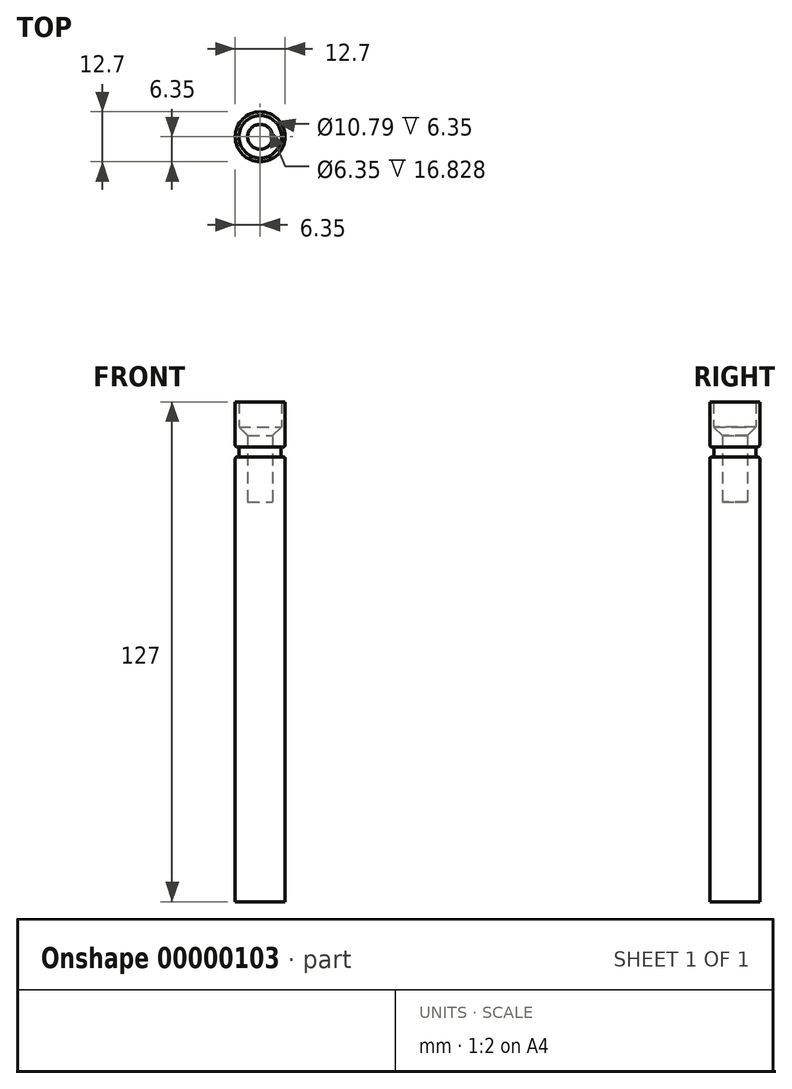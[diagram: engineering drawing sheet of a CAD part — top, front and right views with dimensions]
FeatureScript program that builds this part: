
annotation { "Feature Type Name" : "Feature", "Feature Type Description" : "" }
export const myFeature = defineFeature(function(context is Context, id is Id, definition is map)
    precondition{}
    {
        {
            var Q0;
            Q0=qCreatedBy(makeId("Top.planeOp"),FACE);
            var sketch = newSketch(context, id + "F0", { "sketchPlane" : qUnion([Q0])});
            skCircle(sketch, "E0", {"center": v(0, 0) * mm, "radius": 6.35 * mm});
            skSolve(sketch);
        }
        {
            var Q0;
            Q0=makeQuery(id+"F0.imprint","IMPRINT",FACE,{"disambiguationData":[TD([[makeQuery(id+"F0.imprint","IMPRINT",EDGE,{"derivedFrom":sQuery(id+"F0.wireOp",EDGE,"E0")}),1.0]])]});
            extrude(context, id + "F1", {"entities" : qUnion([Q0]), "depth" : 127 * mm});
        }
        {
            var Q0;
            Q0=qCreatedBy(makeId("Front.planeOp"),FACE);
            var sketch = newSketch(context, id + "F2", { "sketchPlane" : qUnion([Q0])});
            skLineSegment(sketch, "E1.rect.bottom", {"start": v(7.37, 115.57) * mm, "end": v(5.33, 115.57) * mm});
            skLineSegment(sketch, "E1.rect.top", {"start": v(7.37, 113.03) * mm, "end": v(5.33, 113.03) * mm});
            skLineSegment(sketch, "E1.rect.left", {"start": v(7.37, 115.57) * mm, "end": v(7.37, 113.03) * mm});
            skLineSegment(sketch, "E1.rect.right", {"start": v(5.33, 115.57) * mm, "end": v(5.33, 113.03) * mm});
            skPoint(sketch, "E1.rect.middle", {"position": v(6.35, 114.3) * mm});
            skLineSegment(sketch, "E2", {"start": v(0, 127.05) * mm, "end": v(0, 0) * mm, "construction": true});
            skSolve(sketch);
        }
        {
            var Q0;
            Q0=makeQuery(id+"F2.imprint","IMPRINT",FACE,{"disambiguationData":[TD([[makeQuery(id+"F2.imprint","IMPRINT",EDGE,{"derivedFrom":sQuery(id+"F2.wireOp",EDGE,"E1.rect.bottom")}),1.0]])]});
            var Q1;
            Q1=sQuery(id+"F2.wireOp",EDGE,"E2");
            revolve(context, id + "F3", {"operationType" : NewBodyOperationType.REMOVE, "entities" : qUnion([Q0]), "axis" : qUnion([Q1]), "revolveType" : RevolveType.FULL, "oppositeDirection" : true});
        }
        {
            var Q0;
            Q0=makeQuery(id+"F3.opRevolve","SWEPT_EDGE",EDGE,{"disambiguationData":[OSD([sQuery(id+"F2.wireOp",EDGE,"E1.rect.bottom"),sQuery(id+"F2.wireOp",EDGE,"E1.rect.right")])]});
            var Q1;
            Q1=makeQuery(id+"F3.opRevolve","SWEPT_EDGE",EDGE,{"disambiguationData":[OSD([sQuery(id+"F2.wireOp",EDGE,"E1.rect.top"),sQuery(id+"F2.wireOp",EDGE,"E1.rect.right")])]});
            var Q2;
            Q2=makeQuery(id+"F3.boolean.opBoolean","INTERSECT",EDGE,{"derivedFrom":[makeQuery(id+"F1.opExtrude","SWEPT_FACE",FACE,{"disambiguationData":[OSD([sQuery(id+"F0.wireOp",EDGE,"E0")])]}),makeQuery(id+"F3.opRevolve","SWEPT_FACE",FACE,{"disambiguationData":[OSD([sQuery(id+"F2.wireOp",EDGE,"E1.rect.bottom")])]})]});
            var Q3;
            Q3=makeQuery(id+"F3.boolean.opBoolean","INTERSECT",EDGE,{"derivedFrom":[makeQuery(id+"F1.opExtrude","SWEPT_FACE",FACE,{"disambiguationData":[OSD([sQuery(id+"F0.wireOp",EDGE,"E0")])]}),makeQuery(id+"F3.opRevolve","SWEPT_FACE",FACE,{"disambiguationData":[OSD([sQuery(id+"F2.wireOp",EDGE,"E1.rect.top")])]})]});
            fillet(context, id + "F4", {"entities" : qUnion([Q0, Q1, Q2, Q3]), "radius" : 0.5 * mm, "tangentPropagation" : true, "allowEdgeOverflow" : false});
        }
        {
            var Q0;
            Q0=qCreatedBy(makeId("Front.planeOp"),FACE);
            var sketch = newSketch(context, id + "F5", { "sketchPlane" : qUnion([Q0])});
            skLineSegment(sketch, "E3", {"start": v(0, 127) * mm, "end": v(0, 0) * mm, "construction": true});
            skLineSegment(sketch, "E4", {"start": v(5.4, 127) * mm, "end": v(5.4, 120.65) * mm});
            skLineSegment(sketch, "E5", {"start": v(5.4, 120.65) * mm, "end": v(3.17, 118.43) * mm});
            skLineSegment(sketch, "E6", {"start": v(3.17, 118.43) * mm, "end": v(3.17, 101.6) * mm});
            skLineSegment(sketch, "E7", {"start": v(3.17, 101.6) * mm, "end": v(0, 101.6) * mm});
            skLineSegment(sketch, "E8", {"start": v(0, 101.6) * mm, "end": v(0, 127) * mm});
            skLineSegment(sketch, "E9", {"start": v(5.4, 127) * mm, "end": v(0, 127) * mm});
            skSolve(sketch);
        }
        {
            var Q0;
            Q0=makeQuery(id+"F5.imprint","IMPRINT",FACE,{"disambiguationData":[TD([[makeQuery(id+"F5.imprint","IMPRINT",EDGE,{"derivedFrom":sQuery(id+"F5.wireOp",EDGE,"E4")}),-1.0]])]});
            var Q1;
            Q1=sQuery(id+"F5.wireOp",EDGE,"E3");
            revolve(context, id + "F6", {"operationType" : NewBodyOperationType.REMOVE, "entities" : qUnion([Q0]), "axis" : qUnion([Q1]), "revolveType" : RevolveType.FULL, "oppositeDirection" : true});
        }
    });
